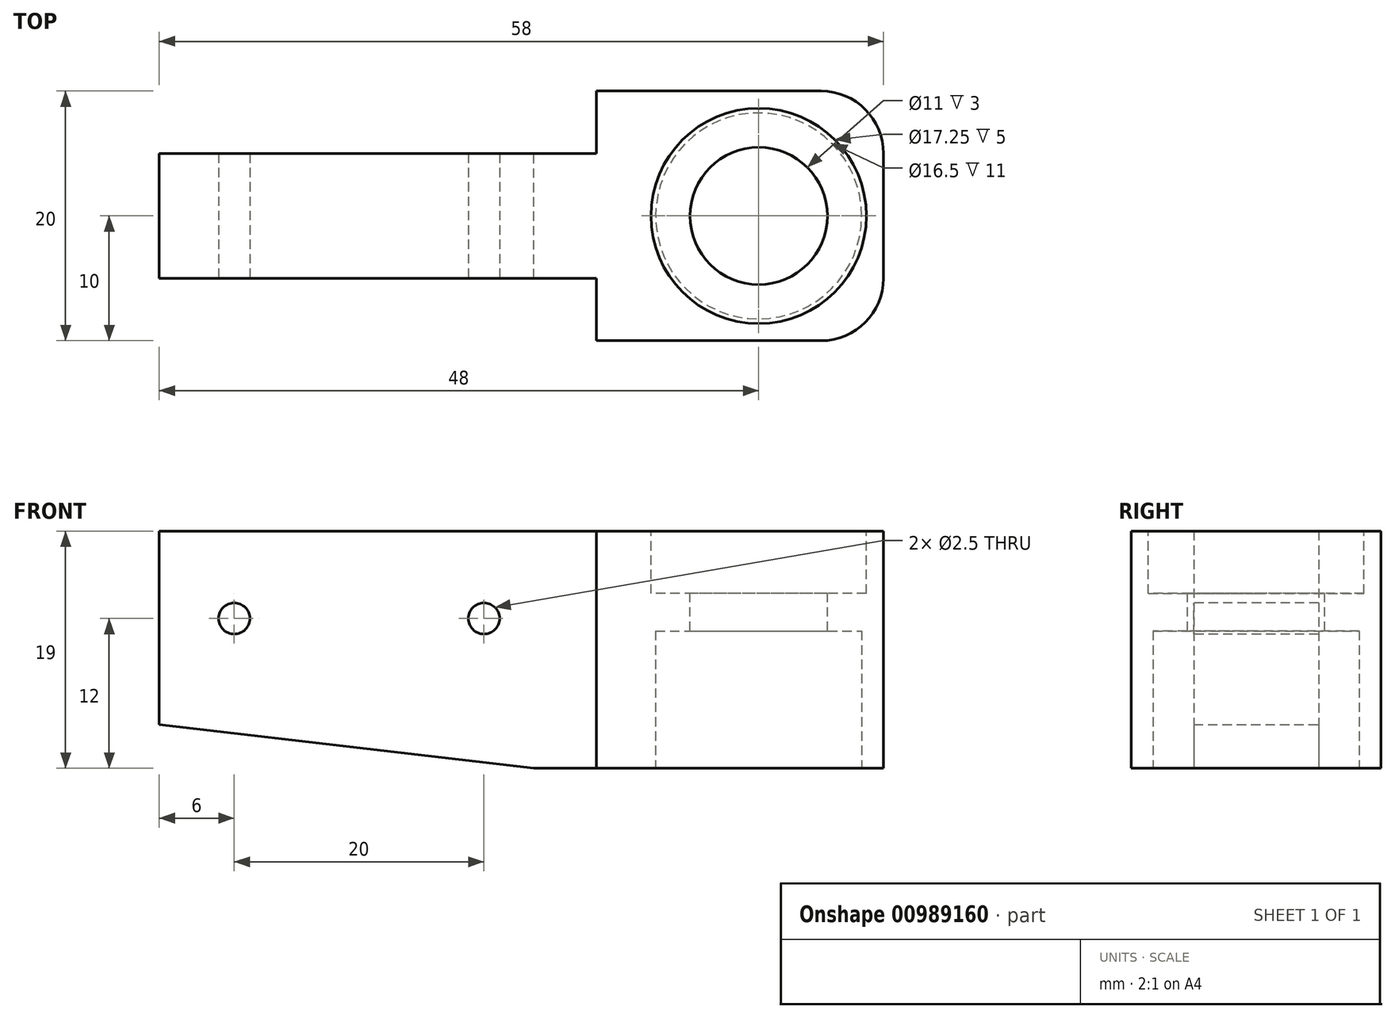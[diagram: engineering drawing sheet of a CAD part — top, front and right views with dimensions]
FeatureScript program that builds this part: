
annotation { "Feature Type Name" : "Feature", "Feature Type Description" : "" }
export const myFeature = defineFeature(function(context is Context, id is Id, definition is map)
    precondition{}
    {
        {
            var Q0;
            Q0=qCreatedBy(makeId("Front.planeOp"),FACE);
            var sketch = newSketch(context, id + "F0", { "sketchPlane" : qUnion([Q0])});
            skLineSegment(sketch, "E0", {"start": v(0, 0) * mm, "end": v(58, 0) * mm});
            skLineSegment(sketch, "E1", {"start": v(58, 0) * mm, "end": v(58, -19) * mm});
            skLineSegment(sketch, "E2", {"start": v(58, -19) * mm, "end": v(30, -19) * mm});
            skLineSegment(sketch, "E3", {"start": v(0, 0) * mm, "end": v(0, -15.5) * mm});
            skLineSegment(sketch, "E4", {"start": v(0, -15.5) * mm, "end": v(30, -19) * mm});
            skSolve(sketch);
        }
        {
            var Q0;
            Q0=makeQuery(id+"F0.imprint","IMPRINT",FACE,{"disambiguationData":[TD([[makeQuery(id+"F0.imprint","IMPRINT",EDGE,{"derivedFrom":sQuery(id+"F0.wireOp",EDGE,"E0")}),-1.0]])]});
            extrude(context, id + "F1", {"entities" : qUnion([Q0]), "depth" : 20 * mm, "offsetDistance" : 25 * mm});
        }
        {
            var Q0;
            Q0=makeQuery(id+"F1.opExtrude","SWEPT_FACE",FACE,{"disambiguationData":[OSD([sQuery(id+"F0.wireOp",EDGE,"E0")])]});
            var sketch = newSketch(context, id + "F2", { "sketchPlane" : qUnion([Q0])});
            skPoint(sketch, "E5", {"position": v(48, -10) * mm});
            skPoint(sketch, "E5.positionSnap0", {"position": v(58, -10) * mm});
            skSolve(sketch);
        }
        {
            var Q0;
            Q0=sQuery(id+"F2.wireOp",VERTEX,"E5");
            var Q1;
            Q1=makeQuery(id+"F1.opExtrude","SWEPT_BODY",BODY,{"disambiguationData":[OSD([sQuery(id+"F0.wireOp",EDGE,"E0"),sQuery(id+"F0.wireOp",EDGE,"E1"),sQuery(id+"F0.wireOp",EDGE,"E2"),sQuery(id+"F0.wireOp",EDGE,"E3"),sQuery(id+"F0.wireOp",EDGE,"E4")])]});
            hole(context, id + "F3", {"style" : HoleStyle.C_BORE, "endStyle" : HoleEndStyle.THROUGH, "holeDiameter" : 11 * mm, "cBoreDiameter" : 17.25 * mm, "cBoreDepth" : 5 * mm, "majorDiameter" : 5 * mm, "isTappedThrough" : true, "tappedDepth" : 5.6 * mm, "tapClearance" : 3, "startFromSketch" : true, "locations" : qUnion([Q0]), "scope" : qUnion([Q1])});
        }
        {
            var Q0;
            Q0=makeQuery(id+"F1.opExtrude","SWEPT_FACE",FACE,{"disambiguationData":[OSD([sQuery(id+"F0.wireOp",EDGE,"E2")])]});
            var sketch = newSketch(context, id + "F4", { "sketchPlane" : qUnion([Q0])});
            skPoint(sketch, "E6", {"position": v(48, 10) * mm});
            skCircle(sketch, "E7", {"center": v(48, 10) * mm, "radius": 8.25 * mm});
            skSolve(sketch);
        }
        {
            var Q0;
            Q0 = qSketchRegion(id + "F4", true);
            extrude(context, id + "F5", {"entities" : qUnion([Q0]), "operationType" : NewBodyOperationType.REMOVE, "oppositeDirection" : true, "depth" : 11 * mm, "offsetDistance" : 25 * mm});
        }
        {
            var Q0;
            Q0=makeQuery(id+"F1.opExtrude","CAP_FACE",FACE,{"disambiguationData":[OSD([sQuery(id+"F0.wireOp",EDGE,"E0"),sQuery(id+"F0.wireOp",EDGE,"E1"),sQuery(id+"F0.wireOp",EDGE,"E2"),sQuery(id+"F0.wireOp",EDGE,"E3"),sQuery(id+"F0.wireOp",EDGE,"E4")])],"isStart":false});
            var sketch = newSketch(context, id + "F6", { "sketchPlane" : qUnion([Q0])});
            skPoint(sketch, "E8", {"position": v(35, 0) * mm});
            skLineSegment(sketch, "E9.bottom", {"start": v(35, 0) * mm, "end": v(-3.73, 0) * mm});
            skLineSegment(sketch, "E9.top", {"start": v(35, -20.37) * mm, "end": v(-3.73, -20.37) * mm});
            skLineSegment(sketch, "E9.left", {"start": v(35, 0) * mm, "end": v(35, -20.37) * mm});
            skLineSegment(sketch, "E9.right", {"start": v(-3.73, 0) * mm, "end": v(-3.73, -20.37) * mm});
            skSolve(sketch);
        }
        {
            var Q0;
            {var subQ1=makeQuery(id+"F1.opExtrude","CAP_EDGE",EDGE,{"disambiguationData":[OSD([sQuery(id+"F0.wireOp",EDGE,"E3")])],"isStart":false});Q0=makeQuery(id+"F6.imprint","IMPRINT",FACE,{"disambiguationData":[TD([[makeQuery(id+"F6.imprint","IMPRINT",EDGE,{"derivedFrom":subQ1}),1.0]])]});}
            extrude(context, id + "F7", {"entities" : qUnion([Q0]), "operationType" : NewBodyOperationType.REMOVE, "oppositeDirection" : true, "depth" : 5 * mm, "offsetDistance" : 25 * mm});
        }
        {
            var Q0;
            Q0=makeQuery(id+"F1.opExtrude","CAP_FACE",FACE,{"disambiguationData":[OSD([sQuery(id+"F0.wireOp",EDGE,"E0"),sQuery(id+"F0.wireOp",EDGE,"E1"),sQuery(id+"F0.wireOp",EDGE,"E2"),sQuery(id+"F0.wireOp",EDGE,"E3"),sQuery(id+"F0.wireOp",EDGE,"E4")])],"isStart":true});
            var sketch = newSketch(context, id + "F8", { "sketchPlane" : qUnion([Q0])});
            skPoint(sketch, "E10", {"position": v(-35, 0) * mm});
            skLineSegment(sketch, "E11.bottom", {"start": v(-35, 0) * mm, "end": v(16.98, 0) * mm});
            skLineSegment(sketch, "E11.top", {"start": v(-35, -24.52) * mm, "end": v(16.98, -24.52) * mm});
            skLineSegment(sketch, "E11.left", {"start": v(-35, 0) * mm, "end": v(-35, -24.52) * mm});
            skLineSegment(sketch, "E11.right", {"start": v(16.98, 0) * mm, "end": v(16.98, -24.52) * mm});
            skSolve(sketch);
        }
        {
            var Q0;
            {var subQ1=makeQuery(id+"F1.opExtrude","CAP_EDGE",EDGE,{"disambiguationData":[OSD([sQuery(id+"F0.wireOp",EDGE,"E3")])],"isStart":true});Q0=makeQuery(id+"F8.imprint","IMPRINT",FACE,{"disambiguationData":[TD([[makeQuery(id+"F8.imprint","IMPRINT",EDGE,{"derivedFrom":subQ1}),-1.0]])]});}
            extrude(context, id + "F9", {"entities" : qUnion([Q0]), "operationType" : NewBodyOperationType.REMOVE, "oppositeDirection" : true, "depth" : 5 * mm, "offsetDistance" : 25 * mm});
        }
        {
            var Q0;
            Q0=makeQuery(id+"F7.boolean.opBoolean","COPY",FACE,{"derivedFrom":makeQuery(id+"F7.opExtrude","CAP_FACE",FACE,{"disambiguationData":[OSD([sQuery(id+"F0.wireOp",EDGE,"E2"),sQuery(id+"F0.wireOp",EDGE,"E3"),sQuery(id+"F0.wireOp",EDGE,"E4"),sQuery(id+"F6.wireOp",EDGE,"E9.bottom"),sQuery(id+"F6.wireOp",EDGE,"E9.left")])],"isStart":false})});
            var sketch = newSketch(context, id + "F10", { "sketchPlane" : qUnion([Q0])});
            skPoint(sketch, "E12", {"position": v(0, -7) * mm});
            skPoint(sketch, "E13", {"position": v(6, -7) * mm});
            skPoint(sketch, "E14", {"position": v(26, -7) * mm});
            skSolve(sketch);
        }
        {
            var Q0;
            Q0=sQuery(id+"F10.wireOp",VERTEX,"E13");
            var Q1;
            Q1=sQuery(id+"F10.wireOp",VERTEX,"E14");
            var Q2;
            Q2=makeQuery(id+"F1.opExtrude","SWEPT_BODY",BODY,{"disambiguationData":[OSD([sQuery(id+"F0.wireOp",EDGE,"E0"),sQuery(id+"F0.wireOp",EDGE,"E1"),sQuery(id+"F0.wireOp",EDGE,"E2"),sQuery(id+"F0.wireOp",EDGE,"E3"),sQuery(id+"F0.wireOp",EDGE,"E4")])]});
            hole(context, id + "F11", {"style" : HoleStyle.SIMPLE, "endStyle" : HoleEndStyle.THROUGH, "standardTappedOrClearance" : lookupTablePath({ "standard" : "ISO", "engagement" : "75%", "pitch" : "0.5 mm", "size" : "M3", "type" : "Tapped" }), "standardBlindInLast" : lookupTablePath({ "standard" : "ISO", "fit" : "Normal", "engagement" : "75%", "pitch" : "0.5 mm", "size" : "M3", "type" : "Clearance & tapped" }), "holeDiameter" : 2.5 * mm, "majorDiameter" : 3 * mm, "showTappedDepth" : true, "isTappedThrough" : true, "tappedDepth" : 5.6 * mm, "tapClearance" : 3, "startFromSketch" : true, "locations" : qUnion([Q0, Q1]), "scope" : qUnion([Q2])});
        }
        {
            var Q0;
            Q0=makeQuery(id+"F1.opExtrude","CAP_EDGE",EDGE,{"disambiguationData":[OSD([sQuery(id+"F0.wireOp",EDGE,"E1")])],"isStart":false});
            var Q1;
            Q1=makeQuery(id+"F1.opExtrude","CAP_EDGE",EDGE,{"disambiguationData":[OSD([sQuery(id+"F0.wireOp",EDGE,"E1")])],"isStart":true});
            fillet(context, id + "F12", {"entities" : qUnion([Q0, Q1]), "radius" : 5 * mm, "tangentPropagation" : true, "allowEdgeOverflow" : false});
        }
    });
